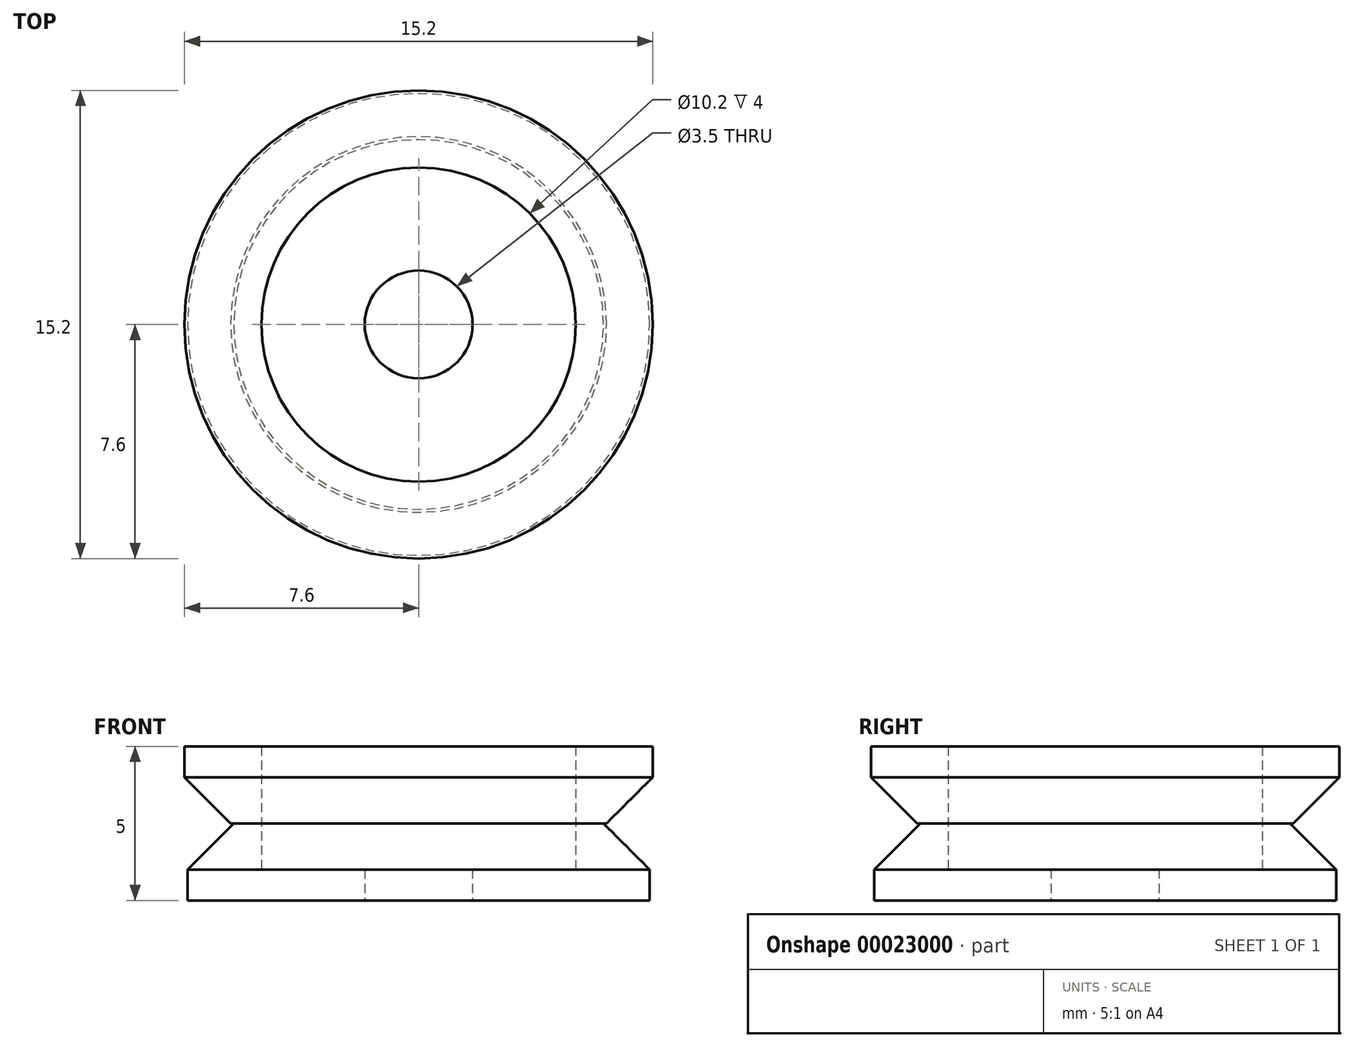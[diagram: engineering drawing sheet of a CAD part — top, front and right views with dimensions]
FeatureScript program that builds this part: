
annotation { "Feature Type Name" : "Feature", "Feature Type Description" : "" }
export const myFeature = defineFeature(function(context is Context, id is Id, definition is map)
    precondition{}
    {
        {
            var Q0;
            Q0=qCreatedBy(makeId("Top.planeOp"),FACE);
            var sketch = newSketch(context, id + "F0", { "sketchPlane" : qUnion([Q0])});
            skCircle(sketch, "E0", {"center": v(0, 0) * mm, "radius": 7.5 * mm});
            skCircle(sketch, "E1", {"center": v(0, 0) * mm, "radius": 1.75 * mm});
            skCircle(sketch, "E2", {"center": v(0, 0) * mm, "radius": 5.1 * mm});
            skSolve(sketch);
        }
        {
            var Q0;
            Q0 = qSketchRegion(id + "F0", true);
            extrude(context, id + "F1", {"entities" : qUnion([Q0]), "depth" : 2.5 * mm});
        }
        {
            var Q0;
            Q0=makeQuery(id+"F0.imprint","IMPRINT",FACE,{"disambiguationData":[TD([[makeQuery(id+"F0.imprint","IMPRINT",EDGE,{"derivedFrom":sQuery(id+"F0.wireOp",EDGE,"E1")}),-1.0]])]});
            extrude(context, id + "F2", {"entities" : qUnion([Q0]), "operationType" : NewBodyOperationType.ADD, "depth" : 1 * mm});
        }
        {
            var Q0;
            Q0=makeQuery(id+"F1.opExtrude","CAP_EDGE",EDGE,{"disambiguationData":[OSD([sQuery(id+"F0.wireOp",EDGE,"E0")])],"isStart":false});
            chamfer(context, id + "F3", {"entities" : qUnion([Q0]), "width" : 1.5 * mm, "tangentPropagation" : true});
        }
        {
            var Q0;
            Q0=makeQuery(id+"F1.opExtrude","CAP_FACE",FACE,{"disambiguationData":[OSD([sQuery(id+"F0.wireOp",EDGE,"E0"),sQuery(id+"F0.wireOp",EDGE,"E2")])],"isStart":false});
            var sketch = newSketch(context, id + "F4", { "sketchPlane" : qUnion([Q0])});
            skCircle(sketch, "E3.0", {"center": v(0, 0) * mm, "radius": 7.6 * mm});
            skSolve(sketch);
        }
        {
            var Q0;
            Q0=makeQuery(id+"F4.imprint","IMPRINT",FACE,{"disambiguationData":[TD([[makeQuery(id+"F4.imprint","IMPRINT",EDGE,{"derivedFrom":sQuery(id+"F4.wireOp",EDGE,"E3.0")}),1.0]])]});
            var Q1;
            {var subQ1=sQuery(id+"F0.wireOp",EDGE,"E2");Q1=makeQuery(id+"F4.imprint","IMPRINT",FACE,{"disambiguationData":[TD([[makeQuery(id+"F4.imprint","IMPRINT",EDGE,{"derivedFrom":makeQuery(id+"F1.opExtrude","CAP_EDGE",EDGE,{"disambiguationData":[OSD([subQ1])],"isStart":false})}),-1.0]])]});}
            extrude(context, id + "F5", {"entities" : qUnion([Q0, Q1]), "operationType" : NewBodyOperationType.ADD, "depth" : 2.5 * mm});
        }
        {
            var Q0;
            Q0=makeQuery(id+"F5.opExtrude","CAP_EDGE",EDGE,{"disambiguationData":[OSD([sQuery(id+"F4.wireOp",EDGE,"E3.0")])],"isStart":true});
            chamfer(context, id + "F6", {"entities" : qUnion([Q0]), "width" : 1.5 * mm, "tangentPropagation" : true});
        }
    });
